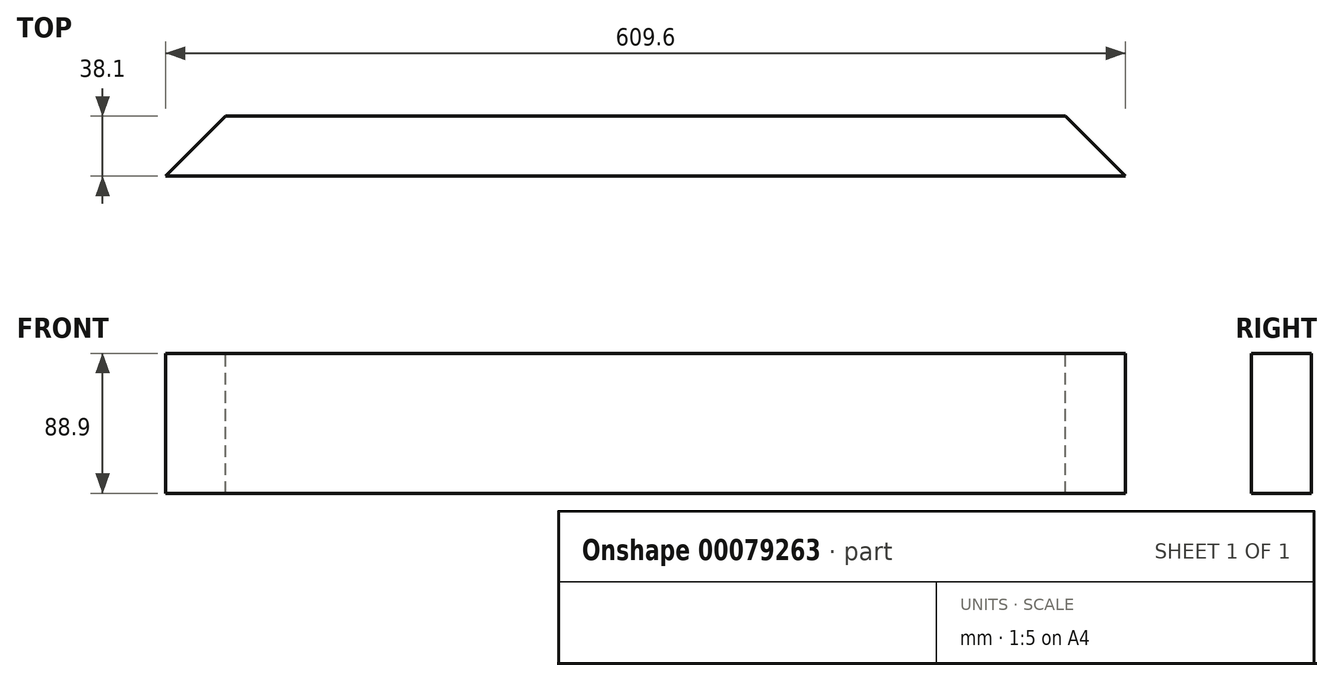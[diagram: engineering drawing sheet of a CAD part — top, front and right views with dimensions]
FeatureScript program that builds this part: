
annotation { "Feature Type Name" : "Feature", "Feature Type Description" : "" }
export const myFeature = defineFeature(function(context is Context, id is Id, definition is map)
    precondition{}
    {
        {
            var Q0;
            Q0=qCreatedBy(makeId("Right.planeOp"),FACE);
            var sketch = newSketch(context, id + "F0", { "sketchPlane" : qUnion([Q0])});
            skLineSegment(sketch, "E0.bottom", {"start": v(0, 0) * mm, "end": v(-38.1, 0) * mm});
            skLineSegment(sketch, "E0.top", {"start": v(0, 88.9) * mm, "end": v(-38.1, 88.9) * mm});
            skLineSegment(sketch, "E0.left", {"start": v(0, 0) * mm, "end": v(0, 88.9) * mm});
            skLineSegment(sketch, "E0.right", {"start": v(-38.1, 0) * mm, "end": v(-38.1, 88.9) * mm});
            skSolve(sketch);
        }
        {
            var Q0;
            Q0=makeQuery(id+"F0.imprint","IMPRINT",FACE,{"disambiguationData":[TD([[makeQuery(id+"F0.imprint","IMPRINT",EDGE,{"derivedFrom":sQuery(id+"F0.wireOp",EDGE,"E0.bottom")}),-1.0]])]});
            extrude(context, id + "F1", {"entities" : qUnion([Q0]), "depth" : 609.6 * mm});
        }
        {
            var Q0;
            Q0=makeQuery(id+"F1.opExtrude","SWEPT_FACE",FACE,{"disambiguationData":[OSD([sQuery(id+"F0.wireOp",EDGE,"E0.top")])]});
            var sketch = newSketch(context, id + "F2", { "sketchPlane" : qUnion([Q0])});
            skLineSegment(sketch, "E1", {"start": v(0, -38.1) * mm, "end": v(38.1, 0) * mm});
            skLineSegment(sketch, "E2", {"start": v(38.1, 0) * mm, "end": v(0, 0) * mm});
            skLineSegment(sketch, "E3", {"start": v(0, 0) * mm, "end": v(0, -38.1) * mm});
            skLineSegment(sketch, "E4", {"start": v(609.6, -38.1) * mm, "end": v(609.6, 0) * mm});
            skLineSegment(sketch, "E5", {"start": v(609.6, 0) * mm, "end": v(571.5, 0) * mm});
            skLineSegment(sketch, "E6", {"start": v(571.5, 0) * mm, "end": v(609.6, -38.1) * mm});
            skSolve(sketch);
        }
        {
            var Q0;
            Q0 = qSketchRegion(id + "F2", true);
            extrude(context, id + "F3", {"entities" : qUnion([Q0]), "operationType" : NewBodyOperationType.REMOVE, "oppositeDirection" : true, "depth" : 88.9 * mm});
        }
    });
